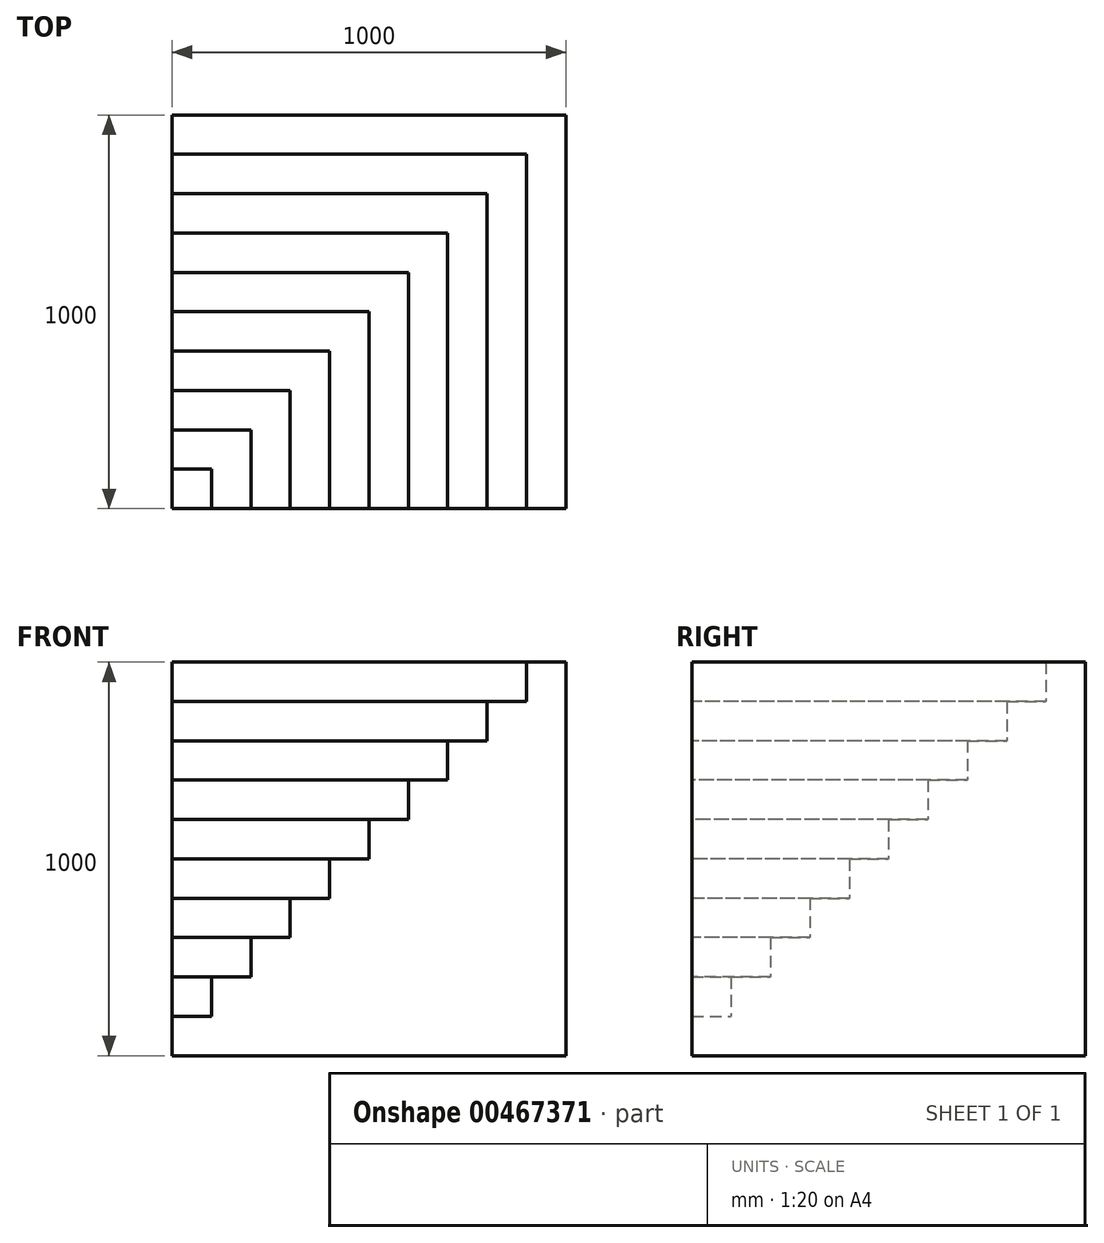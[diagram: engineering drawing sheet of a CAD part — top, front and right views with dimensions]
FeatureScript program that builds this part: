
annotation { "Feature Type Name" : "Feature", "Feature Type Description" : "" }
export const myFeature = defineFeature(function(context is Context, id is Id, definition is map)
    precondition{}
    {
        {
            var Q0;
            Q0=qCreatedBy(makeId("Top.planeOp"),FACE);
            var sketch = newSketch(context, id + "F0", { "sketchPlane" : qUnion([Q0])});
            skLineSegment(sketch, "E0.bottom", {"start": v(0, 0) * mm, "end": v(100, 0) * mm});
            skLineSegment(sketch, "E0.top", {"start": v(0, 100) * mm, "end": v(100, 100) * mm});
            skLineSegment(sketch, "E0.left", {"start": v(0, 0) * mm, "end": v(0, 100) * mm});
            skLineSegment(sketch, "E0.right", {"start": v(100, 0) * mm, "end": v(100, 100) * mm});
            skLineSegment(sketch, "E1", {"start": v(0, 100) * mm, "end": v(0, 200) * mm});
            skLineSegment(sketch, "E2", {"start": v(0, 200) * mm, "end": v(0, 300) * mm});
            skLineSegment(sketch, "E3", {"start": v(0, 300) * mm, "end": v(0, 400) * mm});
            skLineSegment(sketch, "E4", {"start": v(0, 400) * mm, "end": v(0, 500) * mm});
            skLineSegment(sketch, "E5", {"start": v(0, 500) * mm, "end": v(0, 600) * mm});
            skLineSegment(sketch, "E6", {"start": v(0, 600) * mm, "end": v(0, 700) * mm});
            skLineSegment(sketch, "E7", {"start": v(0, 700) * mm, "end": v(0, 800) * mm});
            skLineSegment(sketch, "E8", {"start": v(0, 800) * mm, "end": v(0, 900) * mm});
            skLineSegment(sketch, "E9", {"start": v(0, 900) * mm, "end": v(0, 1000) * mm});
            skLineSegment(sketch, "E10", {"start": v(100, 0) * mm, "end": v(200, 0) * mm});
            skLineSegment(sketch, "E11", {"start": v(200, 0) * mm, "end": v(300, 0) * mm});
            skLineSegment(sketch, "E12", {"start": v(300, 0) * mm, "end": v(400, 0) * mm});
            skLineSegment(sketch, "E13", {"start": v(400, 0) * mm, "end": v(500, 0) * mm});
            skLineSegment(sketch, "E14", {"start": v(500, 0) * mm, "end": v(600, 0) * mm});
            skLineSegment(sketch, "E15", {"start": v(600, 0) * mm, "end": v(700, 0) * mm});
            skLineSegment(sketch, "E16", {"start": v(700, 0) * mm, "end": v(800, 0) * mm});
            skLineSegment(sketch, "E17", {"start": v(800, 0) * mm, "end": v(900, 0) * mm});
            skLineSegment(sketch, "E18", {"start": v(900, 0) * mm, "end": v(1000, 0) * mm});
            skLineSegment(sketch, "E19", {"start": v(0, 200) * mm, "end": v(200, 200) * mm});
            skLineSegment(sketch, "E20", {"start": v(200, 200) * mm, "end": v(200, 0) * mm});
            skLineSegment(sketch, "E21", {"start": v(0, 300) * mm, "end": v(300, 300) * mm});
            skLineSegment(sketch, "E22", {"start": v(300, 300) * mm, "end": v(300, 0) * mm});
            skLineSegment(sketch, "E23", {"start": v(0, 400) * mm, "end": v(400, 400) * mm});
            skLineSegment(sketch, "E24", {"start": v(400, 400) * mm, "end": v(400, 0) * mm});
            skLineSegment(sketch, "E25", {"start": v(0, 500) * mm, "end": v(500, 500) * mm});
            skLineSegment(sketch, "E26", {"start": v(500, 500) * mm, "end": v(500, 0) * mm});
            skLineSegment(sketch, "E27", {"start": v(0, 600) * mm, "end": v(600, 600) * mm});
            skLineSegment(sketch, "E28", {"start": v(600, 600) * mm, "end": v(600, 0) * mm});
            skLineSegment(sketch, "E29", {"start": v(0, 700) * mm, "end": v(700, 700) * mm});
            skLineSegment(sketch, "E30", {"start": v(700, 700) * mm, "end": v(700, 0) * mm});
            skLineSegment(sketch, "E31", {"start": v(0, 800) * mm, "end": v(800, 800) * mm});
            skLineSegment(sketch, "E32", {"start": v(800, 800) * mm, "end": v(800, 0) * mm});
            skLineSegment(sketch, "E33", {"start": v(0, 900) * mm, "end": v(900, 900) * mm});
            skLineSegment(sketch, "E34", {"start": v(900, 900) * mm, "end": v(900, 0) * mm});
            skLineSegment(sketch, "E35", {"start": v(0, 1000) * mm, "end": v(1000, 1000) * mm});
            skLineSegment(sketch, "E36", {"start": v(1000, 1000) * mm, "end": v(1000, 0) * mm});
            skSolve(sketch);
        }
        {
            var Q0;
            Q0=makeQuery(id+"F0.imprint","IMPRINT",FACE,{"disambiguationData":[TD([[makeQuery(id+"F0.imprint","IMPRINT",EDGE,{"derivedFrom":sQuery(id+"F0.wireOp",EDGE,"E9")}),-1.0]])]});
            extrude(context, id + "F1", {"entities" : qUnion([Q0]), "depth" : 1000 * mm});
        }
        {
            var Q0;
            Q0=makeQuery(id+"F0.imprint","IMPRINT",FACE,{"disambiguationData":[TD([[makeQuery(id+"F0.imprint","IMPRINT",EDGE,{"derivedFrom":sQuery(id+"F0.wireOp",EDGE,"E8")}),-1.0]])]});
            extrude(context, id + "F2", {"entities" : qUnion([Q0]), "operationType" : NewBodyOperationType.ADD, "depth" : 900 * mm});
        }
        {
            var Q0;
            Q0=makeQuery(id+"F0.imprint","IMPRINT",FACE,{"disambiguationData":[TD([[makeQuery(id+"F0.imprint","IMPRINT",EDGE,{"derivedFrom":sQuery(id+"F0.wireOp",EDGE,"E7")}),-1.0]])]});
            extrude(context, id + "F3", {"entities" : qUnion([Q0]), "operationType" : NewBodyOperationType.ADD, "depth" : 800 * mm});
        }
        {
            var Q0;
            Q0=makeQuery(id+"F0.imprint","IMPRINT",FACE,{"disambiguationData":[TD([[makeQuery(id+"F0.imprint","IMPRINT",EDGE,{"derivedFrom":sQuery(id+"F0.wireOp",EDGE,"E6")}),-1.0]])]});
            extrude(context, id + "F4", {"entities" : qUnion([Q0]), "operationType" : NewBodyOperationType.ADD, "depth" : 700 * mm});
        }
        {
            var Q0;
            Q0=makeQuery(id+"F0.imprint","IMPRINT",FACE,{"disambiguationData":[TD([[makeQuery(id+"F0.imprint","IMPRINT",EDGE,{"derivedFrom":sQuery(id+"F0.wireOp",EDGE,"E5")}),-1.0]])]});
            extrude(context, id + "F5", {"entities" : qUnion([Q0]), "operationType" : NewBodyOperationType.ADD, "depth" : 600 * mm});
        }
        {
            var Q0;
            Q0=makeQuery(id+"F0.imprint","IMPRINT",FACE,{"disambiguationData":[TD([[makeQuery(id+"F0.imprint","IMPRINT",EDGE,{"derivedFrom":sQuery(id+"F0.wireOp",EDGE,"E4")}),-1.0]])]});
            extrude(context, id + "F6", {"entities" : qUnion([Q0]), "operationType" : NewBodyOperationType.ADD, "depth" : 500 * mm});
        }
        {
            var Q0;
            Q0=makeQuery(id+"F0.imprint","IMPRINT",FACE,{"disambiguationData":[TD([[makeQuery(id+"F0.imprint","IMPRINT",EDGE,{"derivedFrom":sQuery(id+"F0.wireOp",EDGE,"E3")}),-1.0]])]});
            extrude(context, id + "F7", {"entities" : qUnion([Q0]), "operationType" : NewBodyOperationType.ADD, "depth" : 400 * mm});
        }
        {
            var Q0;
            Q0=makeQuery(id+"F0.imprint","IMPRINT",FACE,{"disambiguationData":[TD([[makeQuery(id+"F0.imprint","IMPRINT",EDGE,{"derivedFrom":sQuery(id+"F0.wireOp",EDGE,"E2")}),-1.0]])]});
            extrude(context, id + "F8", {"entities" : qUnion([Q0]), "operationType" : NewBodyOperationType.ADD, "depth" : 300 * mm});
        }
        {
            var Q0;
            Q0=makeQuery(id+"F0.imprint","IMPRINT",FACE,{"disambiguationData":[TD([[makeQuery(id+"F0.imprint","IMPRINT",EDGE,{"derivedFrom":sQuery(id+"F0.wireOp",EDGE,"E0.top")}),1.0]])]});
            extrude(context, id + "F9", {"entities" : qUnion([Q0]), "operationType" : NewBodyOperationType.ADD, "depth" : 200 * mm});
        }
        {
            var Q0;
            Q0=makeQuery(id+"F0.imprint","IMPRINT",FACE,{"disambiguationData":[TD([[makeQuery(id+"F0.imprint","IMPRINT",EDGE,{"derivedFrom":sQuery(id+"F0.wireOp",EDGE,"E0.bottom")}),1.0]])]});
            extrude(context, id + "F10", {"entities" : qUnion([Q0]), "operationType" : NewBodyOperationType.ADD, "depth" : 100 * mm});
        }
    });
